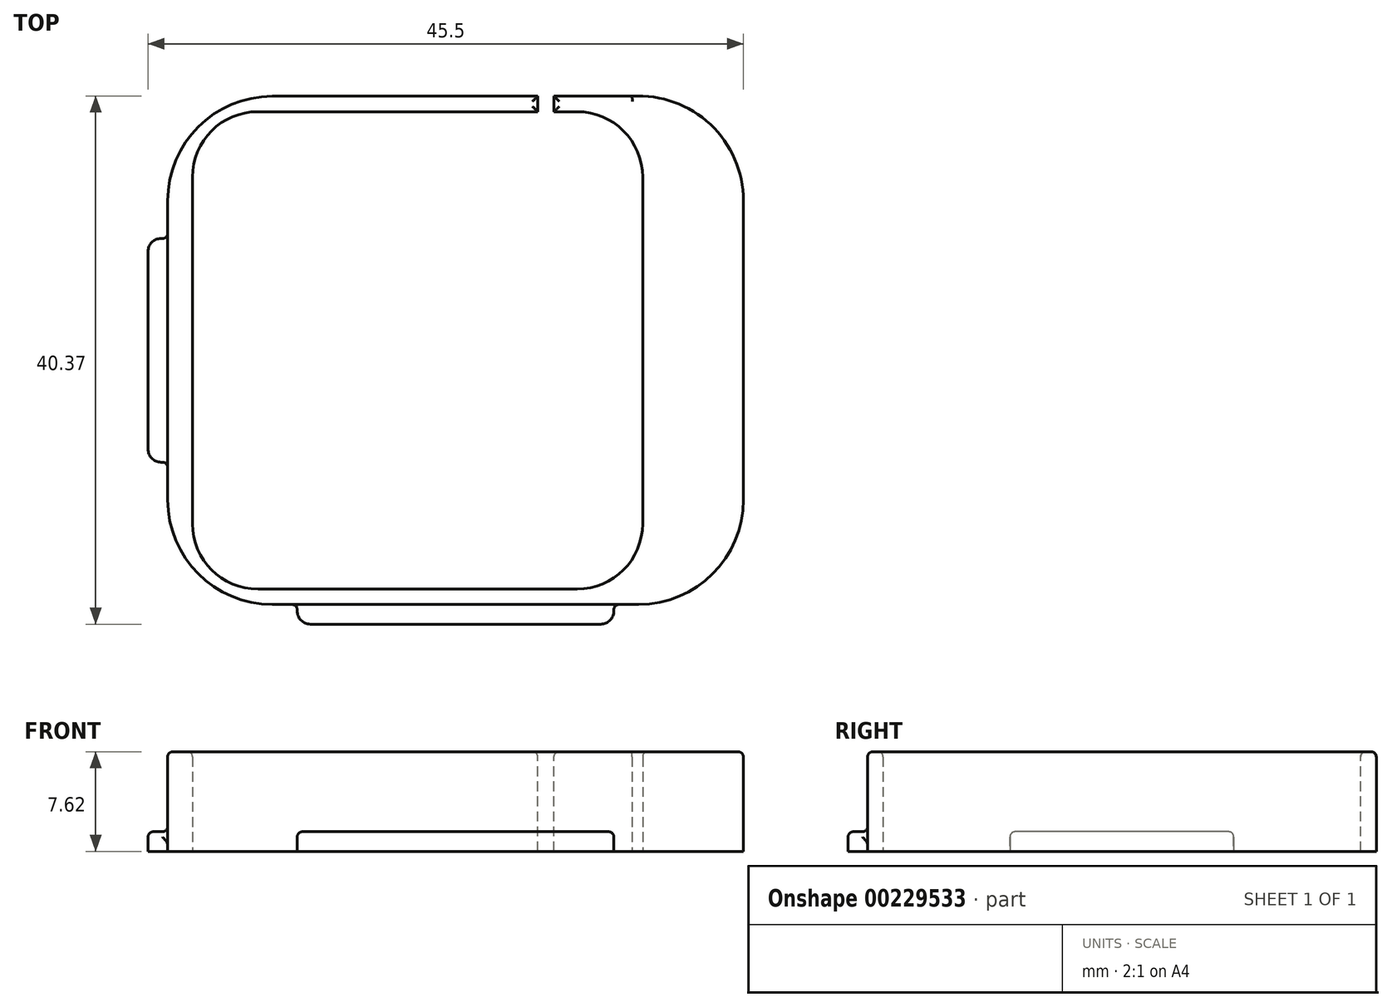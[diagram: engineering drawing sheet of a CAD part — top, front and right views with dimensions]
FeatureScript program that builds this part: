
annotation { "Feature Type Name" : "Feature", "Feature Type Description" : "" }
export const myFeature = defineFeature(function(context is Context, id is Id, definition is map)
    precondition{}
    {
        {
            var Q0;
            Q0=qCreatedBy(makeId("Top.planeOp"),FACE);
            var sketch = newSketch(context, id + "F0", { "sketchPlane" : qUnion([Q0])});
            skLineSegment(sketch, "E0.top", {"start": v(-36, 0) * mm, "end": v(-8, 0) * mm});
            skLineSegment(sketch, "E0.left", {"start": v(-44, 30.86) * mm, "end": v(-44, 8) * mm});
            skLineSegment(sketch, "E0.right", {"start": v(0, 30.87) * mm, "end": v(0, 8) * mm});
            skLineSegment(sketch, "E1.bottom", {"start": v(-12.7, 37.68) * mm, "end": v(-37.1, 37.68) * mm});
            skLineSegment(sketch, "E1.top", {"start": v(-12.7, 1.18) * mm, "end": v(-37.1, 1.18) * mm});
            skLineSegment(sketch, "E1.left", {"start": v(-7.7, 32.68) * mm, "end": v(-7.7, 6.18) * mm});
            skLineSegment(sketch, "E1.right", {"start": v(-42.1, 32.68) * mm, "end": v(-42.1, 6.18) * mm});
            skPoint(sketch, "E2.visualSharp", {"position": v(-42.1, 37.68) * mm});
            skPoint(sketch, "E3.visualSharp", {"position": v(-42.1, 1.18) * mm});
            skArc(sketch, "E3.filletArc", {"start": v(-42.1, 6.18) * mm, "mid": v(-40.64, 2.64) * mm, "end": v(-37.1, 1.18) * mm});
            skPoint(sketch, "E4.visualSharp", {"position": v(-7.7, 1.18) * mm});
            skArc(sketch, "E4.filletArc", {"start": v(-12.7, 1.18) * mm, "mid": v(-9.16, 2.64) * mm, "end": v(-7.7, 6.18) * mm});
            skPoint(sketch, "E5.visualSharp", {"position": v(-7.7, 37.68) * mm});
            skArc(sketch, "E5.filletArc", {"start": v(-7.7, 32.68) * mm, "mid": v(-9.16, 36.21) * mm, "end": v(-12.7, 37.68) * mm});
            skPoint(sketch, "E6.visualSharp", {"position": v(-44, 0) * mm});
            skArc(sketch, "E6.filletArc", {"start": v(-44, 8) * mm, "mid": v(-41.66, 2.34) * mm, "end": v(-36, 0) * mm});
            skPoint(sketch, "E7.visualSharp", {"position": v(-44, 39.7) * mm});
            skArc(sketch, "E7.filletArc", {"start": v(-36, 38.86) * mm, "mid": v(-41.66, 36.52) * mm, "end": v(-44, 30.86) * mm});
            skPoint(sketch, "E8.visualSharp", {"position": v(0, 39.7) * mm});
            skArc(sketch, "E8.filletArc", {"start": v(0, 30.87) * mm, "mid": v(-2.52, 36.7) * mm, "end": v(-8.5, 38.86) * mm});
            skPoint(sketch, "E9.visualSharp", {"position": v(0, 0) * mm});
            skArc(sketch, "E9.filletArc", {"start": v(-8, 0) * mm, "mid": v(-2.34, 2.34) * mm, "end": v(0, 8) * mm});
            skLineSegment(sketch, "E10", {"start": v(-36, 38.86) * mm, "end": v(-8.5, 38.86) * mm});
            skArc(sketch, "E11.filletArc", {"start": v(-37.1, 37.68) * mm, "mid": v(-40.64, 36.21) * mm, "end": v(-42.1, 32.68) * mm});
            skPoint(sketch, "E12", {"position": v(-42.1, 19.43) * mm});
            skPoint(sketch, "E13", {"position": v(-44, 19.43) * mm});
            skSolve(sketch);
        }
        {
            var Q0;
            Q0=qSketchRegion(id+"F0",true);
            extrude(context, id + "F1", {"entities" : qUnion([Q0]), "depth" : 7.62 * mm});
        }
        {
            var Q0;
            Q0=qCreatedBy(makeId("Top.planeOp"),FACE);
            var sketch = newSketch(context, id + "F2", { "sketchPlane" : qUnion([Q0])});
            skLineSegment(sketch, "E14.0", {"start": v(-44, 30.86) * mm, "end": v(-44, 8) * mm});
            skLineSegment(sketch, "E14.1", {"start": v(-36, 0) * mm, "end": v(-8, 0) * mm});
            skLineSegment(sketch, "E15.bottom", {"start": v(-44, 27.98) * mm, "end": v(-44.5, 27.98) * mm});
            skLineSegment(sketch, "E15.top", {"start": v(-44, 10.88) * mm, "end": v(-44.5, 10.88) * mm});
            skLineSegment(sketch, "E15.left", {"start": v(-44, 27.98) * mm, "end": v(-44, 10.88) * mm});
            skLineSegment(sketch, "E15.right", {"start": v(-45.5, 26.98) * mm, "end": v(-45.5, 11.88) * mm});
            skPoint(sketch, "E16", {"position": v(-45.5, 19.43) * mm});
            skPoint(sketch, "E17.visualSharp", {"position": v(-45.5, 27.98) * mm});
            skArc(sketch, "E17.filletArc", {"start": v(-44.5, 27.98) * mm, "mid": v(-45.2, 27.69) * mm, "end": v(-45.5, 26.98) * mm});
            skPoint(sketch, "E18.visualSharp", {"position": v(-45.5, 10.88) * mm});
            skArc(sketch, "E18.filletArc", {"start": v(-45.5, 11.88) * mm, "mid": v(-45.2, 11.17) * mm, "end": v(-44.5, 10.88) * mm});
            skPoint(sketch, "E19", {"position": v(-44, 19.43) * mm});
            skLineSegment(sketch, "E20.bottom", {"start": v(-34.1, 0) * mm, "end": v(-9.9, 0) * mm});
            skLineSegment(sketch, "E20.top", {"start": v(-33.1, -1.5) * mm, "end": v(-10.9, -1.5) * mm});
            skLineSegment(sketch, "E20.left", {"start": v(-34.1, 0) * mm, "end": v(-34.1, -0.5) * mm});
            skLineSegment(sketch, "E20.right", {"start": v(-9.9, 0) * mm, "end": v(-9.9, -0.5) * mm});
            skPoint(sketch, "E21", {"position": v(-22, 0) * mm});
            skPoint(sketch, "E22", {"position": v(-22, -1.5) * mm});
            skPoint(sketch, "E23.visualSharp", {"position": v(-34.1, -1.5) * mm});
            skArc(sketch, "E23.filletArc", {"start": v(-34.1, -0.5) * mm, "mid": v(-33.8, -1.2) * mm, "end": v(-33.1, -1.5) * mm});
            skPoint(sketch, "E24.visualSharp", {"position": v(-9.9, -1.5) * mm});
            skArc(sketch, "E24.filletArc", {"start": v(-10.9, -1.5) * mm, "mid": v(-10.2, -1.2) * mm, "end": v(-9.9, -0.5) * mm});
            skSolve(sketch);
        }
        {
            var Q0;
            Q0=qSketchRegion(id+"F2",true);
            extrude(context, id + "F3", {"entities" : qUnion([Q0]), "operationType" : NewBodyOperationType.ADD, "depth" : 1.5 * mm});
        }
        {
            var Q0;
            Q0=makeQuery(id+"F1.opExtrude","CAP_FACE",FACE,{"disambiguationData":[OSD([sQuery(id+"F0.wireOp",EDGE,"E0.top"),sQuery(id+"F0.wireOp",EDGE,"E0.left"),sQuery(id+"F0.wireOp",EDGE,"E0.right"),sQuery(id+"F0.wireOp",EDGE,"E1.bottom"),sQuery(id+"F0.wireOp",EDGE,"E1.top"),sQuery(id+"F0.wireOp",EDGE,"E1.left"),sQuery(id+"F0.wireOp",EDGE,"E1.right"),sQuery(id+"F0.wireOp",EDGE,"E3.filletArc"),sQuery(id+"F0.wireOp",EDGE,"E4.filletArc"),sQuery(id+"F0.wireOp",EDGE,"E5.filletArc"),sQuery(id+"F0.wireOp",EDGE,"E6.filletArc"),sQuery(id+"F0.wireOp",EDGE,"E7.filletArc"),sQuery(id+"F0.wireOp",EDGE,"E8.filletArc"),sQuery(id+"F0.wireOp",EDGE,"E9.filletArc"),sQuery(id+"F0.wireOp",EDGE,"E10"),sQuery(id+"F0.wireOp",EDGE,"E11.filletArc")])],"isStart":false});
            var sketch = newSketch(context, id + "F4", { "sketchPlane" : qUnion([Q0])});
            skLineSegment(sketch, "E25.top", {"start": v(-15.72, 38.86) * mm, "end": v(-14.47, 38.86) * mm});
            skLineSegment(sketch, "E25.left", {"start": v(-15.72, 37.68) * mm, "end": v(-15.72, 38.86) * mm});
            skLineSegment(sketch, "E25.right", {"start": v(-14.47, 37.68) * mm, "end": v(-14.47, 38.86) * mm});
            skLineSegment(sketch, "E26", {"start": v(-15.72, 37.68) * mm, "end": v(-14.47, 37.68) * mm});
            skSolve(sketch);
        }
        {
            var Q0;
            Q0=makeQuery(id+"F4.imprint","IMPRINT",FACE,{"disambiguationData":[TD([[makeQuery(id+"F4.imprint","IMPRINT",EDGE,{"derivedFrom":sQuery(id+"F4.wireOp",EDGE,"E25.top")}),-1.0]])]});
            extrude(context, id + "F5", {"entities" : qUnion([Q0]), "operationType" : NewBodyOperationType.REMOVE, "endBound" : BoundingType.UP_TO_NEXT, "oppositeDirection" : true, "depth" : 25 * mm});
        }
        {
            var Q0;
            Q0=makeQuery(id+"F1.opExtrude","CAP_FACE",FACE,{"disambiguationData":[OSD([sQuery(id+"F0.wireOp",EDGE,"E0.bottom"),sQuery(id+"F0.wireOp",EDGE,"E0.top"),sQuery(id+"F0.wireOp",EDGE,"E0.left"),sQuery(id+"F0.wireOp",EDGE,"E0.right"),sQuery(id+"F0.wireOp",EDGE,"E1.bottom"),sQuery(id+"F0.wireOp",EDGE,"E1.top"),sQuery(id+"F0.wireOp",EDGE,"E1.left"),sQuery(id+"F0.wireOp",EDGE,"E1.right"),sQuery(id+"F0.wireOp",EDGE,"E2.filletArc"),sQuery(id+"F0.wireOp",EDGE,"E3.filletArc"),sQuery(id+"F0.wireOp",EDGE,"E4.filletArc"),sQuery(id+"F0.wireOp",EDGE,"E5.filletArc"),sQuery(id+"F0.wireOp",EDGE,"E6.filletArc"),sQuery(id+"F0.wireOp",EDGE,"E7.filletArc"),sQuery(id+"F0.wireOp",EDGE,"E8.filletArc"),sQuery(id+"F0.wireOp",EDGE,"E9.filletArc"),sQuery(id+"F0.wireOp",EDGE,"48H5W9qS-3HcK-PUqK-IWbb-xoK6O8Urumot"),sQuery(id+"F0.wireOp",EDGE,"vPFz91A9-O62w-Qs1o-YT8g-QtWOS9IkvXyY"),sQuery(id+"F0.wireOp",EDGE,"7b654645-a64c-46d4-b28a-97a12fab7d7b"),sQuery(id+"F0.wireOp",EDGE,"E10")])],"isStart":false});
            var Q1;
            Q1=makeQuery(id+"F3.opExtrude","CAP_FACE",FACE,{"disambiguationData":[OSD([sQuery(id+"F2.wireOp",EDGE,"E20.bottom"),sQuery(id+"F2.wireOp",EDGE,"E20.top"),sQuery(id+"F2.wireOp",EDGE,"E20.left"),sQuery(id+"F2.wireOp",EDGE,"E20.right"),sQuery(id+"F2.wireOp",EDGE,"E23.filletArc"),sQuery(id+"F2.wireOp",EDGE,"E24.filletArc")])],"isStart":false});
            var Q2;
            Q2=makeQuery(id+"F3.opExtrude","CAP_FACE",FACE,{"disambiguationData":[OSD([sQuery(id+"F2.wireOp",EDGE,"E15.bottom"),sQuery(id+"F2.wireOp",EDGE,"E15.top"),sQuery(id+"F2.wireOp",EDGE,"E15.left"),sQuery(id+"F2.wireOp",EDGE,"E15.right"),sQuery(id+"F2.wireOp",EDGE,"E17.filletArc"),sQuery(id+"F2.wireOp",EDGE,"E18.filletArc")])],"isStart":false});
            fillet(context, id + "F6", {"entities" : qUnion([Q0, Q1, Q2]), "radius" : 0.4 * mm, "tangentPropagation" : true, "allowEdgeOverflow" : false});
        }
    });
